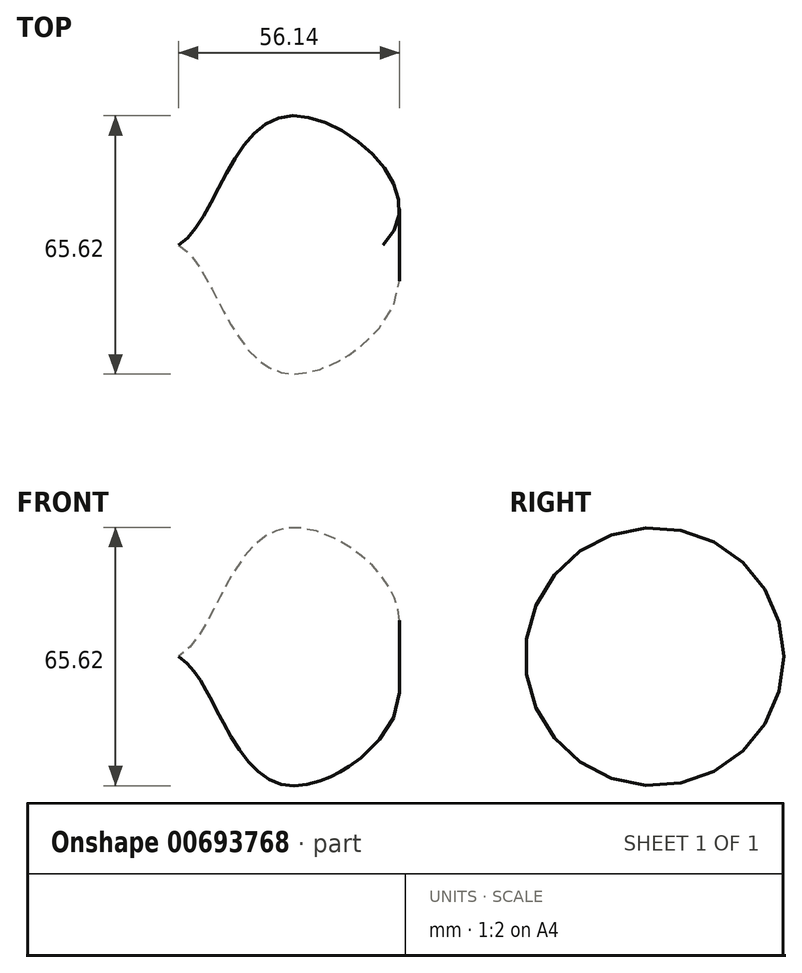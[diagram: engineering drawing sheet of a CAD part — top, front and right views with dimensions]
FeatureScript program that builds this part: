
annotation { "Feature Type Name" : "Feature", "Feature Type Description" : "" }
export const myFeature = defineFeature(function(context is Context, id is Id, definition is map)
    precondition{}
    {
        {
            var Q0;
            Q0=qCreatedBy(makeId("Top.planeOp"),FACE);
            var sketch = newSketch(context, id + "F0", { "sketchPlane" : qUnion([Q0])});
            skFitSpline(sketch, "E0", {"points": [v(0, 0) * mm, v(27.68, 32.71) * mm, v(51.96, 0) * mm], "startDerivative": vector(54.04, 30) * mm, "endDerivative": vector(-84.56, -80.06) * mm});
            skSolve(sketch);
        }
        {
            var Q0;
            Q0=qCreatedBy(makeId("Top.planeOp"),FACE);
            var sketch = newSketch(context, id + "F1", { "sketchPlane" : qUnion([Q0])});
            skLineSegment(sketch, "E1", {"start": v(-12.29, 0) * mm, "end": v(70.02, 0) * mm});
            skSolve(sketch);
        }
        {
            var Q0;
            Q0=sQuery(id+"F0.wireOp",EDGE,"E0");
            var Q1;
            Q1=sQuery(id+"F1.wireOp",EDGE,"E1");
            revolve(context, id + "F2", {"bodyType" : ToolBodyType.SURFACE, "surfaceEntities" : qUnion([Q0]), "axis" : qUnion([Q1]), "revolveType" : RevolveType.FULL, "surfaceOperationType" : NewSurfaceOperationType.NEW});
        }
    });
